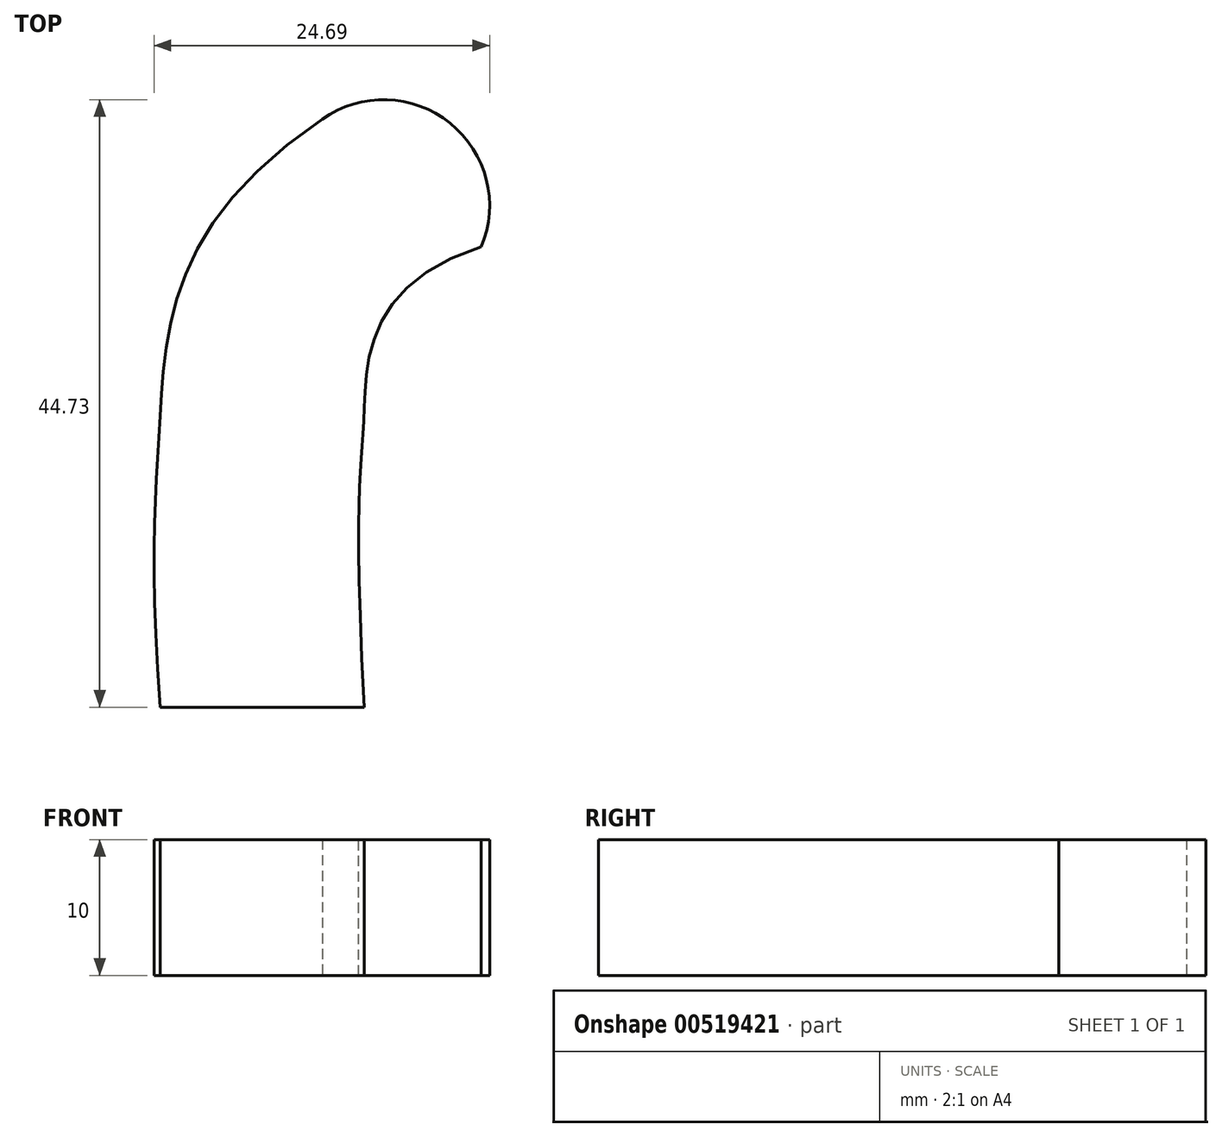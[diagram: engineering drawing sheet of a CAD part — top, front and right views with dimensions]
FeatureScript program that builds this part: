
annotation { "Feature Type Name" : "Feature", "Feature Type Description" : "" }
export const myFeature = defineFeature(function(context is Context, id is Id, definition is map)
    precondition{}
    {
        {
            var Q0;
            Q0=qCreatedBy(makeId("Top.planeOp"),FACE);
            var sketch = newSketch(context, id + "F0", { "sketchPlane" : qUnion([Q0])});
            skLineSegment(sketch, "E0", {"start": v(-53.64, -21.61) * mm, "end": v(-38.64, -21.61) * mm});
            skFitSpline(sketch, "E1", {"points": [v(-53.64, -21.61) * mm, v(-53.64, 0) * mm, v(-41.7, 21.69) * mm], "startDerivative": vector(-4.97, 68.67) * mm, "endDerivative": vector(65.26, 44.14) * mm});
            skFitSpline(sketch, "E2", {"points": [v(-30.02, 12.28) * mm, v(-38.64, 0) * mm, v(-38.64, -21.61) * mm], "startDerivative": vector(-56.9, -17.82) * mm, "endDerivative": vector(4.4, -89.73) * mm});
            skArc(sketch, "E3", {"start": v(-30.02, 12.28) * mm, "mid": v(-32.31, 21.4) * mm, "end": v(-41.7, 21.69) * mm});
            skSolve(sketch);
        }
        {
            var Q0;
            Q0=makeQuery(id+"F0.imprint","IMPRINT",FACE,{"disambiguationData":[TD([[makeQuery(id+"F0.imprint","IMPRINT",EDGE,{"derivedFrom":sQuery(id+"F0.wireOp",EDGE,"E0")}),1.0]])]});
            extrude(context, id + "F1", {"entities" : qUnion([Q0]), "depth" : 10 * mm, "offsetDistance" : 25.4 * mm});
        }
    });
